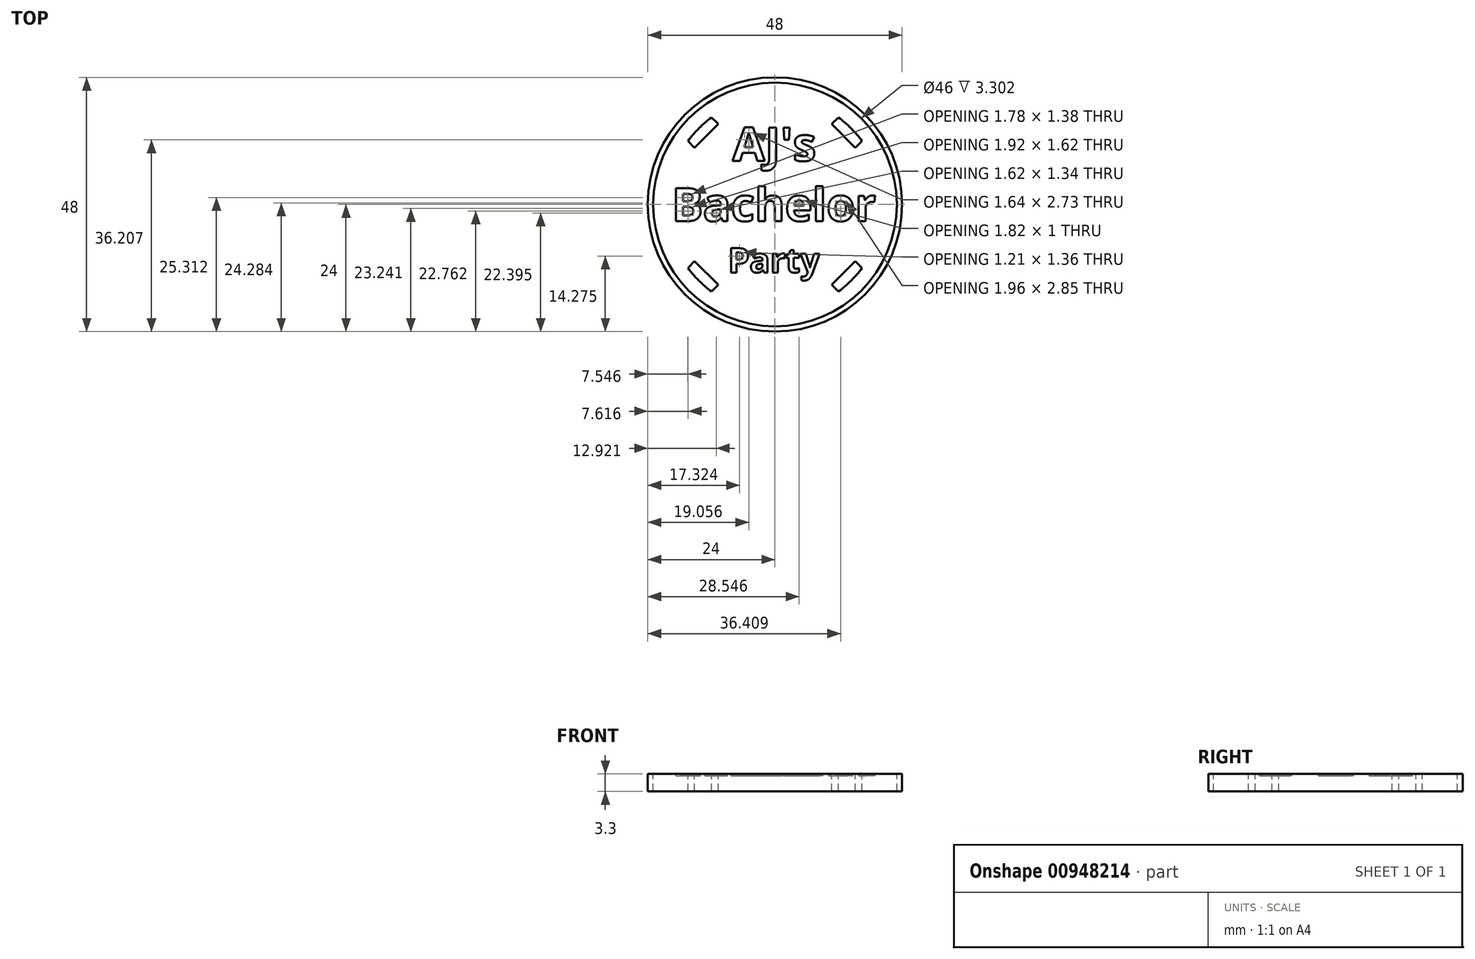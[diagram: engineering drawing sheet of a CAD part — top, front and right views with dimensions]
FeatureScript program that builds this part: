
annotation { "Feature Type Name" : "Feature", "Feature Type Description" : "" }
export const myFeature = defineFeature(function(context is Context, id is Id, definition is map)
    precondition{}
    {
        {
            var Q0;
            Q0=qCreatedBy(makeId("Top.planeOp"),FACE);
            var sketch = newSketch(context, id + "F0", { "sketchPlane" : qUnion([Q0])});
            skText(sketch, "E0", { "text": "Bachelor", "fontName": "OpenSans-Bold.ttf"});
            const initialGuessF0  = {"E0": [-0.01945, -0.00314, 1, 0, 0.00628]};
            skSetInitialGuess(sketch, initialGuessF0);
            skSolve(sketch);
        }
        {
            var Q0;
            Q0=qCreatedBy(makeId("Top.planeOp"),FACE);
            var sketch = newSketch(context, id + "F1", { "sketchPlane" : qUnion([Q0])});
            skText(sketch, "E1", { "text": "AJ\'s", "fontName": "OpenSans-Bold.ttf"});
            const initialGuessF1  = {"E1": [-0.008, 0.00822, 1, 0, 0.00636]};
            skSetInitialGuess(sketch, initialGuessF1);
            skSolve(sketch);
        }
        {
            var Q0;
            Q0=qCreatedBy(makeId("Top.planeOp"),FACE);
            var sketch = newSketch(context, id + "F2", { "sketchPlane" : qUnion([Q0])});
            skText(sketch, "E2", { "text": "Party", "fontName": "OpenSans-Bold.ttf"});
            const initialGuessF2  = {"E2": [-0.00883, -0.01283, 1, 0, 0.00462]};
            skSetInitialGuess(sketch, initialGuessF2);
            skSolve(sketch);
        }
        {
            var Q0;
            Q0=qCreatedBy(makeId("Top.planeOp"),FACE);
            var sketch = newSketch(context, id + "F3", { "sketchPlane" : qUnion([Q0])});
            skLineSegment(sketch, "E3", {"start": v(-14.37, 14.37) * mm, "end": v(14.37, -14.37) * mm, "construction": true});
            skLineSegment(sketch, "E4", {"start": v(-15.18, 10.69) * mm, "end": v(-10.69, 15.18) * mm});
            skLineSegment(sketch, "E5", {"start": v(-10.69, 15.18) * mm, "end": v(-11.95, 16.44) * mm});
            skLineSegment(sketch, "E6", {"start": v(-15.18, 10.69) * mm, "end": v(-16.44, 11.95) * mm});
            skArc(sketch, "E7", {"start": v(-11.95, 16.44) * mm, "mid": v(-14.37, 14.37) * mm, "end": v(-16.44, 11.95) * mm});
            skLineSegment(sketch, "E8.1.0", {"start": v(-15.18, -10.69) * mm, "end": v(-16.44, -11.95) * mm});
            skArc(sketch, "E8.1.1", {"start": v(-16.44, -11.95) * mm, "mid": v(-14.37, -14.37) * mm, "end": v(-11.95, -16.44) * mm});
            skLineSegment(sketch, "E8.1.2", {"start": v(-10.69, -15.18) * mm, "end": v(-11.95, -16.44) * mm});
            skLineSegment(sketch, "E8.1.3", {"start": v(-10.69, -15.18) * mm, "end": v(-15.18, -10.69) * mm});
            skLineSegment(sketch, "E8.2.0", {"start": v(10.69, -15.18) * mm, "end": v(11.95, -16.44) * mm});
            skArc(sketch, "E8.2.1", {"start": v(11.95, -16.44) * mm, "mid": v(14.37, -14.37) * mm, "end": v(16.44, -11.95) * mm});
            skLineSegment(sketch, "E8.2.2", {"start": v(15.18, -10.69) * mm, "end": v(16.44, -11.95) * mm});
            skLineSegment(sketch, "E8.2.3", {"start": v(15.18, -10.69) * mm, "end": v(10.69, -15.18) * mm});
            skLineSegment(sketch, "E8.3.0", {"start": v(15.18, 10.69) * mm, "end": v(16.44, 11.95) * mm});
            skArc(sketch, "E8.3.1", {"start": v(16.44, 11.95) * mm, "mid": v(14.37, 14.37) * mm, "end": v(11.95, 16.44) * mm});
            skLineSegment(sketch, "E8.3.2", {"start": v(10.69, 15.18) * mm, "end": v(11.95, 16.44) * mm});
            skLineSegment(sketch, "E8.3.3", {"start": v(10.69, 15.18) * mm, "end": v(15.18, 10.69) * mm});
            skSolve(sketch);
        }
        {
            var Q0;
            Q0 = qSketchRegion(id + "F0", true);
            var Q1;
            Q1 = qSketchRegion(id + "F1", true);
            var Q2;
            Q2 = qSketchRegion(id + "F2", true);
            extrude(context, id + "F4", {"entities" : qUnion([Q0, Q1, Q2]), "oppositeDirection" : true, "depth" : 0.38 * mm, "offsetDistance" : 25.4 * mm});
        }
        {
            var Q0;
            Q0 = qSketchRegion(id + "F3", true);
            extrude(context, id + "F5", {"entities" : qUnion([Q0]), "oppositeDirection" : true, "depth" : 3.3 * mm, "offsetDistance" : 25.4 * mm});
        }
        {
            var Q0;
            Q0=qCreatedBy(makeId("Top.planeOp"),FACE);
            var sketch = newSketch(context, id + "F6", { "sketchPlane" : qUnion([Q0])});
            skCircle(sketch, "E9", {"center": v(0, 0) * mm, "radius": 23 * mm});
            skCircle(sketch, "E10", {"center": v(0, 0) * mm, "radius": 24 * mm});
            skSolve(sketch);
        }
        {
            var Q0;
            Q0 = qSketchRegion(id + "F6", true);
            extrude(context, id + "F7", {"entities" : qUnion([Q0]), "oppositeDirection" : true, "depth" : 3.3 * mm, "offsetDistance" : 25 * mm});
        }
    });
